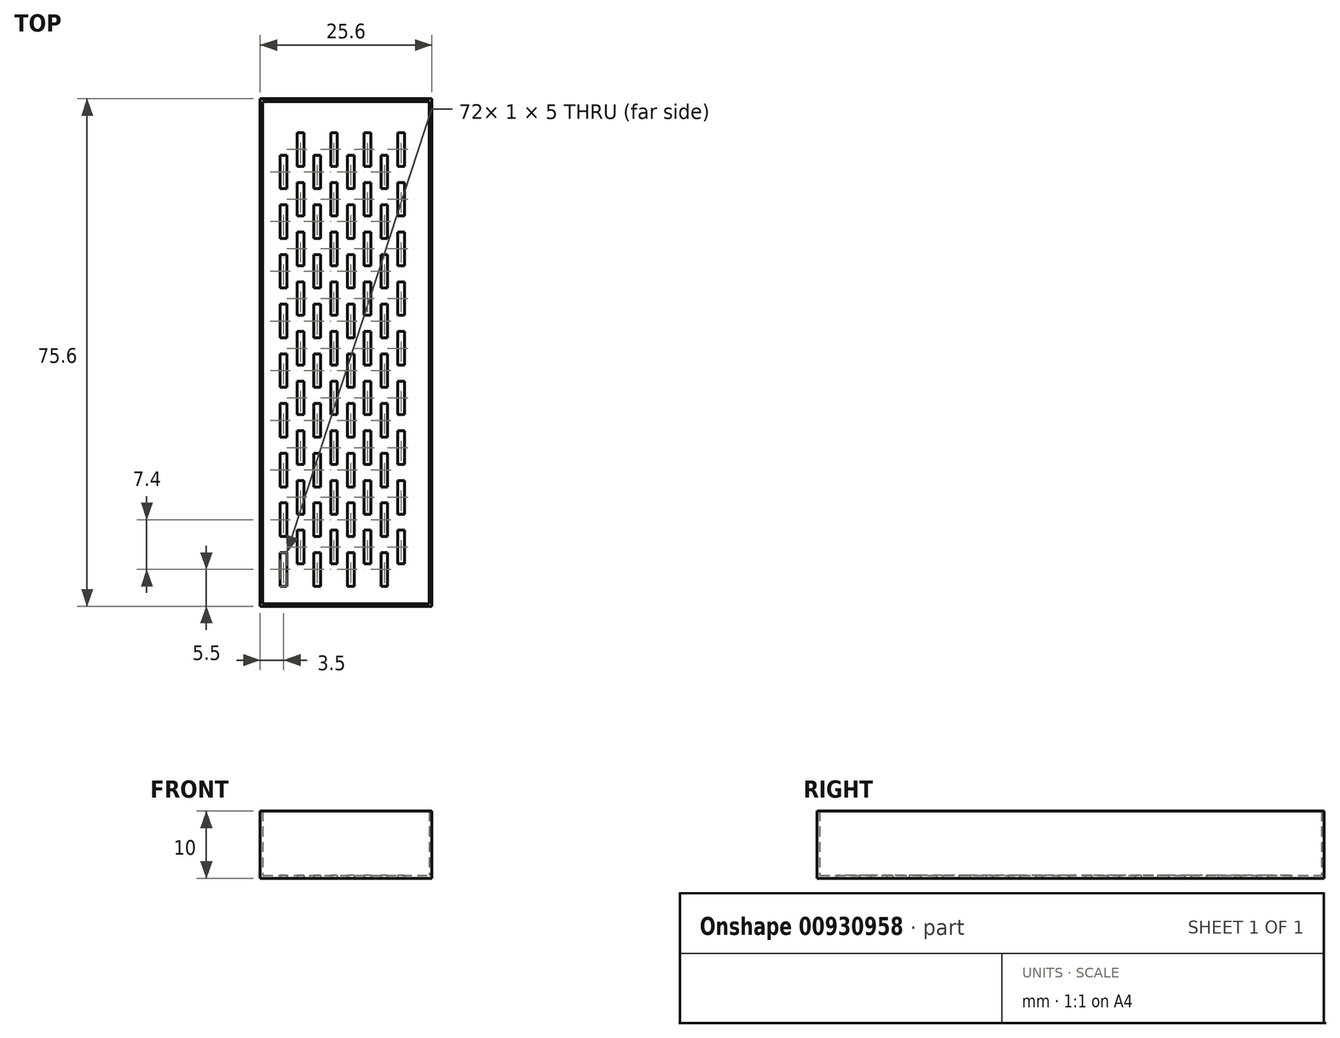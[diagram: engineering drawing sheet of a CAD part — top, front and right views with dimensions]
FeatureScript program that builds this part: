
annotation { "Feature Type Name" : "Feature", "Feature Type Description" : "" }
export const myFeature = defineFeature(function(context is Context, id is Id, definition is map)
    precondition{}
    {
        {
            assignVariable(context, id + "F0", {"name" : "wall", "anyValue" : 0.4});
        }
        {
            var Q0;
            Q0=qCreatedBy(makeId("Top.planeOp"),FACE);
            var sketch = newSketch(context, id + "F1", { "sketchPlane" : qUnion([Q0])});
            skLineSegment(sketch, "E0.bottom", {"start": v(0, 0) * mm, "end": v(25.6, 0) * mm});
            skLineSegment(sketch, "E0.top", {"start": v(0, 75.6) * mm, "end": v(25.6, 75.6) * mm});
            skLineSegment(sketch, "E0.left", {"start": v(0, 0) * mm, "end": v(0, 75.6) * mm});
            skLineSegment(sketch, "E0.right", {"start": v(25.6, 0) * mm, "end": v(25.6, 75.6) * mm});
            skSolve(sketch);
        }
        {
            var Q0;
            Q0 = qSketchRegion(id + "F1", true);
            extrude(context, id + "F2", {"entities" : qUnion([Q0]), "depth" : 10 * mm, "offsetDistance" : 25 * mm});
        }
        {
            var Q0;
            Q0=makeQuery(id+"F2.opExtrude","CAP_FACE",FACE,{"disambiguationData":[OSD([sQuery(id+"F1.wireOp",EDGE,"E0.bottom"),sQuery(id+"F1.wireOp",EDGE,"E0.top"),sQuery(id+"F1.wireOp",EDGE,"E0.left"),sQuery(id+"F1.wireOp",EDGE,"E0.right")])],"isStart":false});
            shell(context, id + "F3", {"entities" : qUnion([Q0]), "thickness" : (getVariable(context, 'wall')) * mm});
        }
        {
            var Q0;
            Q0=makeQuery(id+"F2.opExtrude","CAP_FACE",FACE,{"disambiguationData":[OSD([sQuery(id+"F1.wireOp",EDGE,"E0.bottom"),sQuery(id+"F1.wireOp",EDGE,"E0.top"),sQuery(id+"F1.wireOp",EDGE,"E0.left"),sQuery(id+"F1.wireOp",EDGE,"E0.right")])],"isStart":true});
            var sketch = newSketch(context, id + "F4", { "sketchPlane" : qUnion([Q0])});
            skLineSegment(sketch, "E1.bottom", {"start": v(3, -3) * mm, "end": v(4, -3) * mm});
            skLineSegment(sketch, "E1.top", {"start": v(3, -8) * mm, "end": v(4, -8) * mm});
            skLineSegment(sketch, "E1.left", {"start": v(3, -3) * mm, "end": v(3, -8) * mm});
            skLineSegment(sketch, "E1.right", {"start": v(4, -3) * mm, "end": v(4, -8) * mm});
            skLineSegment(sketch, "E2.bottom", {"start": v(5.5, -6.33) * mm, "end": v(6.5, -6.33) * mm});
            skLineSegment(sketch, "E2.top", {"start": v(5.5, -11.33) * mm, "end": v(6.5, -11.33) * mm});
            skLineSegment(sketch, "E2.left", {"start": v(5.5, -6.33) * mm, "end": v(5.5, -11.33) * mm});
            skLineSegment(sketch, "E2.right", {"start": v(6.5, -6.33) * mm, "end": v(6.5, -11.33) * mm});
            skLineSegment(sketch, "E3.0.1.0", {"start": v(5.5, -13.73) * mm, "end": v(5.5, -18.73) * mm});
            skLineSegment(sketch, "E3.0.1.1", {"start": v(3, -10.4) * mm, "end": v(4, -10.4) * mm});
            skLineSegment(sketch, "E3.0.1.2", {"start": v(6.5, -13.73) * mm, "end": v(6.5, -18.73) * mm});
            skLineSegment(sketch, "E3.0.1.3", {"start": v(5.5, -18.73) * mm, "end": v(6.5, -18.73) * mm});
            skLineSegment(sketch, "E3.0.1.4", {"start": v(5.5, -13.73) * mm, "end": v(6.5, -13.73) * mm});
            skLineSegment(sketch, "E3.0.1.5", {"start": v(3, -10.4) * mm, "end": v(3, -15.4) * mm});
            skLineSegment(sketch, "E3.0.1.6", {"start": v(3, -15.4) * mm, "end": v(4, -15.4) * mm});
            skLineSegment(sketch, "E3.0.1.7", {"start": v(4, -10.4) * mm, "end": v(4, -15.4) * mm});
            skLineSegment(sketch, "E3.0.2.0", {"start": v(5.5, -21.13) * mm, "end": v(5.5, -26.13) * mm});
            skLineSegment(sketch, "E3.0.2.1", {"start": v(3, -17.8) * mm, "end": v(4, -17.8) * mm});
            skLineSegment(sketch, "E3.0.2.2", {"start": v(6.5, -21.13) * mm, "end": v(6.5, -26.13) * mm});
            skLineSegment(sketch, "E3.0.2.3", {"start": v(5.5, -26.13) * mm, "end": v(6.5, -26.13) * mm});
            skLineSegment(sketch, "E3.0.2.4", {"start": v(5.5, -21.13) * mm, "end": v(6.5, -21.13) * mm});
            skLineSegment(sketch, "E3.0.2.5", {"start": v(3, -17.8) * mm, "end": v(3, -22.8) * mm});
            skLineSegment(sketch, "E3.0.2.6", {"start": v(3, -22.8) * mm, "end": v(4, -22.8) * mm});
            skLineSegment(sketch, "E3.0.2.7", {"start": v(4, -17.8) * mm, "end": v(4, -22.8) * mm});
            skLineSegment(sketch, "E3.0.3.0", {"start": v(5.5, -28.53) * mm, "end": v(5.5, -33.53) * mm});
            skLineSegment(sketch, "E3.0.3.1", {"start": v(3, -25.2) * mm, "end": v(4, -25.2) * mm});
            skLineSegment(sketch, "E3.0.3.2", {"start": v(6.5, -28.53) * mm, "end": v(6.5, -33.53) * mm});
            skLineSegment(sketch, "E3.0.3.3", {"start": v(5.5, -33.53) * mm, "end": v(6.5, -33.53) * mm});
            skLineSegment(sketch, "E3.0.3.4", {"start": v(5.5, -28.53) * mm, "end": v(6.5, -28.53) * mm});
            skLineSegment(sketch, "E3.0.3.5", {"start": v(3, -25.2) * mm, "end": v(3, -30.2) * mm});
            skLineSegment(sketch, "E3.0.3.6", {"start": v(3, -30.2) * mm, "end": v(4, -30.2) * mm});
            skLineSegment(sketch, "E3.0.3.7", {"start": v(4, -25.2) * mm, "end": v(4, -30.2) * mm});
            skLineSegment(sketch, "E3.0.4.0", {"start": v(5.5, -35.93) * mm, "end": v(5.5, -40.93) * mm});
            skLineSegment(sketch, "E3.0.4.1", {"start": v(3, -32.6) * mm, "end": v(4, -32.6) * mm});
            skLineSegment(sketch, "E3.0.4.2", {"start": v(6.5, -35.93) * mm, "end": v(6.5, -40.93) * mm});
            skLineSegment(sketch, "E3.0.4.3", {"start": v(5.5, -40.93) * mm, "end": v(6.5, -40.93) * mm});
            skLineSegment(sketch, "E3.0.4.4", {"start": v(5.5, -35.93) * mm, "end": v(6.5, -35.93) * mm});
            skLineSegment(sketch, "E3.0.4.5", {"start": v(3, -32.6) * mm, "end": v(3, -37.6) * mm});
            skLineSegment(sketch, "E3.0.4.6", {"start": v(3, -37.6) * mm, "end": v(4, -37.6) * mm});
            skLineSegment(sketch, "E3.0.4.7", {"start": v(4, -32.6) * mm, "end": v(4, -37.6) * mm});
            skLineSegment(sketch, "E3.0.5.0", {"start": v(5.5, -43.33) * mm, "end": v(5.5, -48.33) * mm});
            skLineSegment(sketch, "E3.0.5.1", {"start": v(3, -40) * mm, "end": v(4, -40) * mm});
            skLineSegment(sketch, "E3.0.5.2", {"start": v(6.5, -43.33) * mm, "end": v(6.5, -48.33) * mm});
            skLineSegment(sketch, "E3.0.5.3", {"start": v(5.5, -48.33) * mm, "end": v(6.5, -48.33) * mm});
            skLineSegment(sketch, "E3.0.5.4", {"start": v(5.5, -43.33) * mm, "end": v(6.5, -43.33) * mm});
            skLineSegment(sketch, "E3.0.5.5", {"start": v(3, -40) * mm, "end": v(3, -45) * mm});
            skLineSegment(sketch, "E3.0.5.6", {"start": v(3, -45) * mm, "end": v(4, -45) * mm});
            skLineSegment(sketch, "E3.0.5.7", {"start": v(4, -40) * mm, "end": v(4, -45) * mm});
            skLineSegment(sketch, "E3.0.6.0", {"start": v(5.5, -50.73) * mm, "end": v(5.5, -55.73) * mm});
            skLineSegment(sketch, "E3.0.6.1", {"start": v(3, -47.4) * mm, "end": v(4, -47.4) * mm});
            skLineSegment(sketch, "E3.0.6.2", {"start": v(6.5, -50.73) * mm, "end": v(6.5, -55.73) * mm});
            skLineSegment(sketch, "E3.0.6.3", {"start": v(5.5, -55.73) * mm, "end": v(6.5, -55.73) * mm});
            skLineSegment(sketch, "E3.0.6.4", {"start": v(5.5, -50.73) * mm, "end": v(6.5, -50.73) * mm});
            skLineSegment(sketch, "E3.0.6.5", {"start": v(3, -47.4) * mm, "end": v(3, -52.4) * mm});
            skLineSegment(sketch, "E3.0.6.6", {"start": v(3, -52.4) * mm, "end": v(4, -52.4) * mm});
            skLineSegment(sketch, "E3.0.6.7", {"start": v(4, -47.4) * mm, "end": v(4, -52.4) * mm});
            skLineSegment(sketch, "E3.0.7.0", {"start": v(5.5, -58.13) * mm, "end": v(5.5, -63.13) * mm});
            skLineSegment(sketch, "E3.0.7.1", {"start": v(3, -54.8) * mm, "end": v(4, -54.8) * mm});
            skLineSegment(sketch, "E3.0.7.2", {"start": v(6.5, -58.13) * mm, "end": v(6.5, -63.13) * mm});
            skLineSegment(sketch, "E3.0.7.3", {"start": v(5.5, -63.13) * mm, "end": v(6.5, -63.13) * mm});
            skLineSegment(sketch, "E3.0.7.4", {"start": v(5.5, -58.13) * mm, "end": v(6.5, -58.13) * mm});
            skLineSegment(sketch, "E3.0.7.5", {"start": v(3, -54.8) * mm, "end": v(3, -59.8) * mm});
            skLineSegment(sketch, "E3.0.7.6", {"start": v(3, -59.8) * mm, "end": v(4, -59.8) * mm});
            skLineSegment(sketch, "E3.0.7.7", {"start": v(4, -54.8) * mm, "end": v(4, -59.8) * mm});
            skLineSegment(sketch, "E3.0.8.0", {"start": v(5.5, -65.53) * mm, "end": v(5.5, -70.53) * mm});
            skLineSegment(sketch, "E3.0.8.1", {"start": v(3, -62.2) * mm, "end": v(4, -62.2) * mm});
            skLineSegment(sketch, "E3.0.8.2", {"start": v(6.5, -65.53) * mm, "end": v(6.5, -70.53) * mm});
            skLineSegment(sketch, "E3.0.8.3", {"start": v(5.5, -70.53) * mm, "end": v(6.5, -70.53) * mm});
            skLineSegment(sketch, "E3.0.8.4", {"start": v(5.5, -65.53) * mm, "end": v(6.5, -65.53) * mm});
            skLineSegment(sketch, "E3.0.8.5", {"start": v(3, -62.2) * mm, "end": v(3, -67.2) * mm});
            skLineSegment(sketch, "E3.0.8.6", {"start": v(3, -67.2) * mm, "end": v(4, -67.2) * mm});
            skLineSegment(sketch, "E3.0.8.7", {"start": v(4, -62.2) * mm, "end": v(4, -67.2) * mm});
            skLineSegment(sketch, "E3.1.0.0", {"start": v(10.5, -6.33) * mm, "end": v(10.5, -11.33) * mm});
            skLineSegment(sketch, "E3.1.0.1", {"start": v(8, -3) * mm, "end": v(9, -3) * mm});
            skLineSegment(sketch, "E3.1.0.2", {"start": v(11.5, -6.33) * mm, "end": v(11.5, -11.33) * mm});
            skLineSegment(sketch, "E3.1.0.3", {"start": v(10.5, -11.33) * mm, "end": v(11.5, -11.33) * mm});
            skLineSegment(sketch, "E3.1.0.4", {"start": v(10.5, -6.33) * mm, "end": v(11.5, -6.33) * mm});
            skLineSegment(sketch, "E3.1.0.5", {"start": v(8, -3) * mm, "end": v(8, -8) * mm});
            skLineSegment(sketch, "E3.1.0.6", {"start": v(8, -8) * mm, "end": v(9, -8) * mm});
            skLineSegment(sketch, "E3.1.0.7", {"start": v(9, -3) * mm, "end": v(9, -8) * mm});
            skLineSegment(sketch, "E3.1.1.0", {"start": v(10.5, -13.73) * mm, "end": v(10.5, -18.73) * mm});
            skLineSegment(sketch, "E3.1.1.1", {"start": v(8, -10.4) * mm, "end": v(9, -10.4) * mm});
            skLineSegment(sketch, "E3.1.1.2", {"start": v(11.5, -13.73) * mm, "end": v(11.5, -18.73) * mm});
            skLineSegment(sketch, "E3.1.1.3", {"start": v(10.5, -18.73) * mm, "end": v(11.5, -18.73) * mm});
            skLineSegment(sketch, "E3.1.1.4", {"start": v(10.5, -13.73) * mm, "end": v(11.5, -13.73) * mm});
            skLineSegment(sketch, "E3.1.1.5", {"start": v(8, -10.4) * mm, "end": v(8, -15.4) * mm});
            skLineSegment(sketch, "E3.1.1.6", {"start": v(8, -15.4) * mm, "end": v(9, -15.4) * mm});
            skLineSegment(sketch, "E3.1.1.7", {"start": v(9, -10.4) * mm, "end": v(9, -15.4) * mm});
            skLineSegment(sketch, "E3.1.2.0", {"start": v(10.5, -21.13) * mm, "end": v(10.5, -26.13) * mm});
            skLineSegment(sketch, "E3.1.2.1", {"start": v(8, -17.8) * mm, "end": v(9, -17.8) * mm});
            skLineSegment(sketch, "E3.1.2.2", {"start": v(11.5, -21.13) * mm, "end": v(11.5, -26.13) * mm});
            skLineSegment(sketch, "E3.1.2.3", {"start": v(10.5, -26.13) * mm, "end": v(11.5, -26.13) * mm});
            skLineSegment(sketch, "E3.1.2.4", {"start": v(10.5, -21.13) * mm, "end": v(11.5, -21.13) * mm});
            skLineSegment(sketch, "E3.1.2.5", {"start": v(8, -17.8) * mm, "end": v(8, -22.8) * mm});
            skLineSegment(sketch, "E3.1.2.6", {"start": v(8, -22.8) * mm, "end": v(9, -22.8) * mm});
            skLineSegment(sketch, "E3.1.2.7", {"start": v(9, -17.8) * mm, "end": v(9, -22.8) * mm});
            skLineSegment(sketch, "E3.1.3.0", {"start": v(10.5, -28.53) * mm, "end": v(10.5, -33.53) * mm});
            skLineSegment(sketch, "E3.1.3.1", {"start": v(8, -25.2) * mm, "end": v(9, -25.2) * mm});
            skLineSegment(sketch, "E3.1.3.2", {"start": v(11.5, -28.53) * mm, "end": v(11.5, -33.53) * mm});
            skLineSegment(sketch, "E3.1.3.3", {"start": v(10.5, -33.53) * mm, "end": v(11.5, -33.53) * mm});
            skLineSegment(sketch, "E3.1.3.4", {"start": v(10.5, -28.53) * mm, "end": v(11.5, -28.53) * mm});
            skLineSegment(sketch, "E3.1.3.5", {"start": v(8, -25.2) * mm, "end": v(8, -30.2) * mm});
            skLineSegment(sketch, "E3.1.3.6", {"start": v(8, -30.2) * mm, "end": v(9, -30.2) * mm});
            skLineSegment(sketch, "E3.1.3.7", {"start": v(9, -25.2) * mm, "end": v(9, -30.2) * mm});
            skLineSegment(sketch, "E3.1.4.0", {"start": v(10.5, -35.93) * mm, "end": v(10.5, -40.93) * mm});
            skLineSegment(sketch, "E3.1.4.1", {"start": v(8, -32.6) * mm, "end": v(9, -32.6) * mm});
            skLineSegment(sketch, "E3.1.4.2", {"start": v(11.5, -35.93) * mm, "end": v(11.5, -40.93) * mm});
            skLineSegment(sketch, "E3.1.4.3", {"start": v(10.5, -40.93) * mm, "end": v(11.5, -40.93) * mm});
            skLineSegment(sketch, "E3.1.4.4", {"start": v(10.5, -35.93) * mm, "end": v(11.5, -35.93) * mm});
            skLineSegment(sketch, "E3.1.4.5", {"start": v(8, -32.6) * mm, "end": v(8, -37.6) * mm});
            skLineSegment(sketch, "E3.1.4.6", {"start": v(8, -37.6) * mm, "end": v(9, -37.6) * mm});
            skLineSegment(sketch, "E3.1.4.7", {"start": v(9, -32.6) * mm, "end": v(9, -37.6) * mm});
            skLineSegment(sketch, "E3.1.5.0", {"start": v(10.5, -43.33) * mm, "end": v(10.5, -48.33) * mm});
            skLineSegment(sketch, "E3.1.5.1", {"start": v(8, -40) * mm, "end": v(9, -40) * mm});
            skLineSegment(sketch, "E3.1.5.2", {"start": v(11.5, -43.33) * mm, "end": v(11.5, -48.33) * mm});
            skLineSegment(sketch, "E3.1.5.3", {"start": v(10.5, -48.33) * mm, "end": v(11.5, -48.33) * mm});
            skLineSegment(sketch, "E3.1.5.4", {"start": v(10.5, -43.33) * mm, "end": v(11.5, -43.33) * mm});
            skLineSegment(sketch, "E3.1.5.5", {"start": v(8, -40) * mm, "end": v(8, -45) * mm});
            skLineSegment(sketch, "E3.1.5.6", {"start": v(8, -45) * mm, "end": v(9, -45) * mm});
            skLineSegment(sketch, "E3.1.5.7", {"start": v(9, -40) * mm, "end": v(9, -45) * mm});
            skLineSegment(sketch, "E3.1.6.0", {"start": v(10.5, -50.73) * mm, "end": v(10.5, -55.73) * mm});
            skLineSegment(sketch, "E3.1.6.1", {"start": v(8, -47.4) * mm, "end": v(9, -47.4) * mm});
            skLineSegment(sketch, "E3.1.6.2", {"start": v(11.5, -50.73) * mm, "end": v(11.5, -55.73) * mm});
            skLineSegment(sketch, "E3.1.6.3", {"start": v(10.5, -55.73) * mm, "end": v(11.5, -55.73) * mm});
            skLineSegment(sketch, "E3.1.6.4", {"start": v(10.5, -50.73) * mm, "end": v(11.5, -50.73) * mm});
            skLineSegment(sketch, "E3.1.6.5", {"start": v(8, -47.4) * mm, "end": v(8, -52.4) * mm});
            skLineSegment(sketch, "E3.1.6.6", {"start": v(8, -52.4) * mm, "end": v(9, -52.4) * mm});
            skLineSegment(sketch, "E3.1.6.7", {"start": v(9, -47.4) * mm, "end": v(9, -52.4) * mm});
            skLineSegment(sketch, "E3.1.7.0", {"start": v(10.5, -58.13) * mm, "end": v(10.5, -63.13) * mm});
            skLineSegment(sketch, "E3.1.7.1", {"start": v(8, -54.8) * mm, "end": v(9, -54.8) * mm});
            skLineSegment(sketch, "E3.1.7.2", {"start": v(11.5, -58.13) * mm, "end": v(11.5, -63.13) * mm});
            skLineSegment(sketch, "E3.1.7.3", {"start": v(10.5, -63.13) * mm, "end": v(11.5, -63.13) * mm});
            skLineSegment(sketch, "E3.1.7.4", {"start": v(10.5, -58.13) * mm, "end": v(11.5, -58.13) * mm});
            skLineSegment(sketch, "E3.1.7.5", {"start": v(8, -54.8) * mm, "end": v(8, -59.8) * mm});
            skLineSegment(sketch, "E3.1.7.6", {"start": v(8, -59.8) * mm, "end": v(9, -59.8) * mm});
            skLineSegment(sketch, "E3.1.7.7", {"start": v(9, -54.8) * mm, "end": v(9, -59.8) * mm});
            skLineSegment(sketch, "E3.1.8.0", {"start": v(10.5, -65.53) * mm, "end": v(10.5, -70.53) * mm});
            skLineSegment(sketch, "E3.1.8.1", {"start": v(8, -62.2) * mm, "end": v(9, -62.2) * mm});
            skLineSegment(sketch, "E3.1.8.2", {"start": v(11.5, -65.53) * mm, "end": v(11.5, -70.53) * mm});
            skLineSegment(sketch, "E3.1.8.3", {"start": v(10.5, -70.53) * mm, "end": v(11.5, -70.53) * mm});
            skLineSegment(sketch, "E3.1.8.4", {"start": v(10.5, -65.53) * mm, "end": v(11.5, -65.53) * mm});
            skLineSegment(sketch, "E3.1.8.5", {"start": v(8, -62.2) * mm, "end": v(8, -67.2) * mm});
            skLineSegment(sketch, "E3.1.8.6", {"start": v(8, -67.2) * mm, "end": v(9, -67.2) * mm});
            skLineSegment(sketch, "E3.1.8.7", {"start": v(9, -62.2) * mm, "end": v(9, -67.2) * mm});
            skLineSegment(sketch, "E3.2.0.0", {"start": v(15.5, -6.33) * mm, "end": v(15.5, -11.33) * mm});
            skLineSegment(sketch, "E3.2.0.1", {"start": v(13, -3) * mm, "end": v(14, -3) * mm});
            skLineSegment(sketch, "E3.2.0.2", {"start": v(16.5, -6.33) * mm, "end": v(16.5, -11.33) * mm});
            skLineSegment(sketch, "E3.2.0.3", {"start": v(15.5, -11.33) * mm, "end": v(16.5, -11.33) * mm});
            skLineSegment(sketch, "E3.2.0.4", {"start": v(15.5, -6.33) * mm, "end": v(16.5, -6.33) * mm});
            skLineSegment(sketch, "E3.2.0.5", {"start": v(13, -3) * mm, "end": v(13, -8) * mm});
            skLineSegment(sketch, "E3.2.0.6", {"start": v(13, -8) * mm, "end": v(14, -8) * mm});
            skLineSegment(sketch, "E3.2.0.7", {"start": v(14, -3) * mm, "end": v(14, -8) * mm});
            skLineSegment(sketch, "E3.2.1.0", {"start": v(15.5, -13.73) * mm, "end": v(15.5, -18.73) * mm});
            skLineSegment(sketch, "E3.2.1.1", {"start": v(13, -10.4) * mm, "end": v(14, -10.4) * mm});
            skLineSegment(sketch, "E3.2.1.2", {"start": v(16.5, -13.73) * mm, "end": v(16.5, -18.73) * mm});
            skLineSegment(sketch, "E3.2.1.3", {"start": v(15.5, -18.73) * mm, "end": v(16.5, -18.73) * mm});
            skLineSegment(sketch, "E3.2.1.4", {"start": v(15.5, -13.73) * mm, "end": v(16.5, -13.73) * mm});
            skLineSegment(sketch, "E3.2.1.5", {"start": v(13, -10.4) * mm, "end": v(13, -15.4) * mm});
            skLineSegment(sketch, "E3.2.1.6", {"start": v(13, -15.4) * mm, "end": v(14, -15.4) * mm});
            skLineSegment(sketch, "E3.2.1.7", {"start": v(14, -10.4) * mm, "end": v(14, -15.4) * mm});
            skLineSegment(sketch, "E3.2.2.0", {"start": v(15.5, -21.13) * mm, "end": v(15.5, -26.13) * mm});
            skLineSegment(sketch, "E3.2.2.1", {"start": v(13, -17.8) * mm, "end": v(14, -17.8) * mm});
            skLineSegment(sketch, "E3.2.2.2", {"start": v(16.5, -21.13) * mm, "end": v(16.5, -26.13) * mm});
            skLineSegment(sketch, "E3.2.2.3", {"start": v(15.5, -26.13) * mm, "end": v(16.5, -26.13) * mm});
            skLineSegment(sketch, "E3.2.2.4", {"start": v(15.5, -21.13) * mm, "end": v(16.5, -21.13) * mm});
            skLineSegment(sketch, "E3.2.2.5", {"start": v(13, -17.8) * mm, "end": v(13, -22.8) * mm});
            skLineSegment(sketch, "E3.2.2.6", {"start": v(13, -22.8) * mm, "end": v(14, -22.8) * mm});
            skLineSegment(sketch, "E3.2.2.7", {"start": v(14, -17.8) * mm, "end": v(14, -22.8) * mm});
            skLineSegment(sketch, "E3.2.3.0", {"start": v(15.5, -28.53) * mm, "end": v(15.5, -33.53) * mm});
            skLineSegment(sketch, "E3.2.3.1", {"start": v(13, -25.2) * mm, "end": v(14, -25.2) * mm});
            skLineSegment(sketch, "E3.2.3.2", {"start": v(16.5, -28.53) * mm, "end": v(16.5, -33.53) * mm});
            skLineSegment(sketch, "E3.2.3.3", {"start": v(15.5, -33.53) * mm, "end": v(16.5, -33.53) * mm});
            skLineSegment(sketch, "E3.2.3.4", {"start": v(15.5, -28.53) * mm, "end": v(16.5, -28.53) * mm});
            skLineSegment(sketch, "E3.2.3.5", {"start": v(13, -25.2) * mm, "end": v(13, -30.2) * mm});
            skLineSegment(sketch, "E3.2.3.6", {"start": v(13, -30.2) * mm, "end": v(14, -30.2) * mm});
            skLineSegment(sketch, "E3.2.3.7", {"start": v(14, -25.2) * mm, "end": v(14, -30.2) * mm});
            skLineSegment(sketch, "E3.2.4.0", {"start": v(15.5, -35.93) * mm, "end": v(15.5, -40.93) * mm});
            skLineSegment(sketch, "E3.2.4.1", {"start": v(13, -32.6) * mm, "end": v(14, -32.6) * mm});
            skLineSegment(sketch, "E3.2.4.2", {"start": v(16.5, -35.93) * mm, "end": v(16.5, -40.93) * mm});
            skLineSegment(sketch, "E3.2.4.3", {"start": v(15.5, -40.93) * mm, "end": v(16.5, -40.93) * mm});
            skLineSegment(sketch, "E3.2.4.4", {"start": v(15.5, -35.93) * mm, "end": v(16.5, -35.93) * mm});
            skLineSegment(sketch, "E3.2.4.5", {"start": v(13, -32.6) * mm, "end": v(13, -37.6) * mm});
            skLineSegment(sketch, "E3.2.4.6", {"start": v(13, -37.6) * mm, "end": v(14, -37.6) * mm});
            skLineSegment(sketch, "E3.2.4.7", {"start": v(14, -32.6) * mm, "end": v(14, -37.6) * mm});
            skLineSegment(sketch, "E3.2.5.0", {"start": v(15.5, -43.33) * mm, "end": v(15.5, -48.33) * mm});
            skLineSegment(sketch, "E3.2.5.1", {"start": v(13, -40) * mm, "end": v(14, -40) * mm});
            skLineSegment(sketch, "E3.2.5.2", {"start": v(16.5, -43.33) * mm, "end": v(16.5, -48.33) * mm});
            skLineSegment(sketch, "E3.2.5.3", {"start": v(15.5, -48.33) * mm, "end": v(16.5, -48.33) * mm});
            skLineSegment(sketch, "E3.2.5.4", {"start": v(15.5, -43.33) * mm, "end": v(16.5, -43.33) * mm});
            skLineSegment(sketch, "E3.2.5.5", {"start": v(13, -40) * mm, "end": v(13, -45) * mm});
            skLineSegment(sketch, "E3.2.5.6", {"start": v(13, -45) * mm, "end": v(14, -45) * mm});
            skLineSegment(sketch, "E3.2.5.7", {"start": v(14, -40) * mm, "end": v(14, -45) * mm});
            skLineSegment(sketch, "E3.2.6.0", {"start": v(15.5, -50.73) * mm, "end": v(15.5, -55.73) * mm});
            skLineSegment(sketch, "E3.2.6.1", {"start": v(13, -47.4) * mm, "end": v(14, -47.4) * mm});
            skLineSegment(sketch, "E3.2.6.2", {"start": v(16.5, -50.73) * mm, "end": v(16.5, -55.73) * mm});
            skLineSegment(sketch, "E3.2.6.3", {"start": v(15.5, -55.73) * mm, "end": v(16.5, -55.73) * mm});
            skLineSegment(sketch, "E3.2.6.4", {"start": v(15.5, -50.73) * mm, "end": v(16.5, -50.73) * mm});
            skLineSegment(sketch, "E3.2.6.5", {"start": v(13, -47.4) * mm, "end": v(13, -52.4) * mm});
            skLineSegment(sketch, "E3.2.6.6", {"start": v(13, -52.4) * mm, "end": v(14, -52.4) * mm});
            skLineSegment(sketch, "E3.2.6.7", {"start": v(14, -47.4) * mm, "end": v(14, -52.4) * mm});
            skLineSegment(sketch, "E3.2.7.0", {"start": v(15.5, -58.13) * mm, "end": v(15.5, -63.13) * mm});
            skLineSegment(sketch, "E3.2.7.1", {"start": v(13, -54.8) * mm, "end": v(14, -54.8) * mm});
            skLineSegment(sketch, "E3.2.7.2", {"start": v(16.5, -58.13) * mm, "end": v(16.5, -63.13) * mm});
            skLineSegment(sketch, "E3.2.7.3", {"start": v(15.5, -63.13) * mm, "end": v(16.5, -63.13) * mm});
            skLineSegment(sketch, "E3.2.7.4", {"start": v(15.5, -58.13) * mm, "end": v(16.5, -58.13) * mm});
            skLineSegment(sketch, "E3.2.7.5", {"start": v(13, -54.8) * mm, "end": v(13, -59.8) * mm});
            skLineSegment(sketch, "E3.2.7.6", {"start": v(13, -59.8) * mm, "end": v(14, -59.8) * mm});
            skLineSegment(sketch, "E3.2.7.7", {"start": v(14, -54.8) * mm, "end": v(14, -59.8) * mm});
            skLineSegment(sketch, "E3.2.8.0", {"start": v(15.5, -65.53) * mm, "end": v(15.5, -70.53) * mm});
            skLineSegment(sketch, "E3.2.8.1", {"start": v(13, -62.2) * mm, "end": v(14, -62.2) * mm});
            skLineSegment(sketch, "E3.2.8.2", {"start": v(16.5, -65.53) * mm, "end": v(16.5, -70.53) * mm});
            skLineSegment(sketch, "E3.2.8.3", {"start": v(15.5, -70.53) * mm, "end": v(16.5, -70.53) * mm});
            skLineSegment(sketch, "E3.2.8.4", {"start": v(15.5, -65.53) * mm, "end": v(16.5, -65.53) * mm});
            skLineSegment(sketch, "E3.2.8.5", {"start": v(13, -62.2) * mm, "end": v(13, -67.2) * mm});
            skLineSegment(sketch, "E3.2.8.6", {"start": v(13, -67.2) * mm, "end": v(14, -67.2) * mm});
            skLineSegment(sketch, "E3.2.8.7", {"start": v(14, -62.2) * mm, "end": v(14, -67.2) * mm});
            skLineSegment(sketch, "E3.3.0.0", {"start": v(20.5, -6.33) * mm, "end": v(20.5, -11.33) * mm});
            skLineSegment(sketch, "E3.3.0.1", {"start": v(18, -3) * mm, "end": v(19, -3) * mm});
            skLineSegment(sketch, "E3.3.0.2", {"start": v(21.5, -6.33) * mm, "end": v(21.5, -11.33) * mm});
            skLineSegment(sketch, "E3.3.0.3", {"start": v(20.5, -11.33) * mm, "end": v(21.5, -11.33) * mm});
            skLineSegment(sketch, "E3.3.0.4", {"start": v(20.5, -6.33) * mm, "end": v(21.5, -6.33) * mm});
            skLineSegment(sketch, "E3.3.0.5", {"start": v(18, -3) * mm, "end": v(18, -8) * mm});
            skLineSegment(sketch, "E3.3.0.6", {"start": v(18, -8) * mm, "end": v(19, -8) * mm});
            skLineSegment(sketch, "E3.3.0.7", {"start": v(19, -3) * mm, "end": v(19, -8) * mm});
            skLineSegment(sketch, "E3.3.1.0", {"start": v(20.5, -13.73) * mm, "end": v(20.5, -18.73) * mm});
            skLineSegment(sketch, "E3.3.1.1", {"start": v(18, -10.4) * mm, "end": v(19, -10.4) * mm});
            skLineSegment(sketch, "E3.3.1.2", {"start": v(21.5, -13.73) * mm, "end": v(21.5, -18.73) * mm});
            skLineSegment(sketch, "E3.3.1.3", {"start": v(20.5, -18.73) * mm, "end": v(21.5, -18.73) * mm});
            skLineSegment(sketch, "E3.3.1.4", {"start": v(20.5, -13.73) * mm, "end": v(21.5, -13.73) * mm});
            skLineSegment(sketch, "E3.3.1.5", {"start": v(18, -10.4) * mm, "end": v(18, -15.4) * mm});
            skLineSegment(sketch, "E3.3.1.6", {"start": v(18, -15.4) * mm, "end": v(19, -15.4) * mm});
            skLineSegment(sketch, "E3.3.1.7", {"start": v(19, -10.4) * mm, "end": v(19, -15.4) * mm});
            skLineSegment(sketch, "E3.3.2.0", {"start": v(20.5, -21.13) * mm, "end": v(20.5, -26.13) * mm});
            skLineSegment(sketch, "E3.3.2.1", {"start": v(18, -17.8) * mm, "end": v(19, -17.8) * mm});
            skLineSegment(sketch, "E3.3.2.2", {"start": v(21.5, -21.13) * mm, "end": v(21.5, -26.13) * mm});
            skLineSegment(sketch, "E3.3.2.3", {"start": v(20.5, -26.13) * mm, "end": v(21.5, -26.13) * mm});
            skLineSegment(sketch, "E3.3.2.4", {"start": v(20.5, -21.13) * mm, "end": v(21.5, -21.13) * mm});
            skLineSegment(sketch, "E3.3.2.5", {"start": v(18, -17.8) * mm, "end": v(18, -22.8) * mm});
            skLineSegment(sketch, "E3.3.2.6", {"start": v(18, -22.8) * mm, "end": v(19, -22.8) * mm});
            skLineSegment(sketch, "E3.3.2.7", {"start": v(19, -17.8) * mm, "end": v(19, -22.8) * mm});
            skLineSegment(sketch, "E3.3.3.0", {"start": v(20.5, -28.53) * mm, "end": v(20.5, -33.53) * mm});
            skLineSegment(sketch, "E3.3.3.1", {"start": v(18, -25.2) * mm, "end": v(19, -25.2) * mm});
            skLineSegment(sketch, "E3.3.3.2", {"start": v(21.5, -28.53) * mm, "end": v(21.5, -33.53) * mm});
            skLineSegment(sketch, "E3.3.3.3", {"start": v(20.5, -33.53) * mm, "end": v(21.5, -33.53) * mm});
            skLineSegment(sketch, "E3.3.3.4", {"start": v(20.5, -28.53) * mm, "end": v(21.5, -28.53) * mm});
            skLineSegment(sketch, "E3.3.3.5", {"start": v(18, -25.2) * mm, "end": v(18, -30.2) * mm});
            skLineSegment(sketch, "E3.3.3.6", {"start": v(18, -30.2) * mm, "end": v(19, -30.2) * mm});
            skLineSegment(sketch, "E3.3.3.7", {"start": v(19, -25.2) * mm, "end": v(19, -30.2) * mm});
            skLineSegment(sketch, "E3.3.4.0", {"start": v(20.5, -35.93) * mm, "end": v(20.5, -40.93) * mm});
            skLineSegment(sketch, "E3.3.4.1", {"start": v(18, -32.6) * mm, "end": v(19, -32.6) * mm});
            skLineSegment(sketch, "E3.3.4.2", {"start": v(21.5, -35.93) * mm, "end": v(21.5, -40.93) * mm});
            skLineSegment(sketch, "E3.3.4.3", {"start": v(20.5, -40.93) * mm, "end": v(21.5, -40.93) * mm});
            skLineSegment(sketch, "E3.3.4.4", {"start": v(20.5, -35.93) * mm, "end": v(21.5, -35.93) * mm});
            skLineSegment(sketch, "E3.3.4.5", {"start": v(18, -32.6) * mm, "end": v(18, -37.6) * mm});
            skLineSegment(sketch, "E3.3.4.6", {"start": v(18, -37.6) * mm, "end": v(19, -37.6) * mm});
            skLineSegment(sketch, "E3.3.4.7", {"start": v(19, -32.6) * mm, "end": v(19, -37.6) * mm});
            skLineSegment(sketch, "E3.3.5.0", {"start": v(20.5, -43.33) * mm, "end": v(20.5, -48.33) * mm});
            skLineSegment(sketch, "E3.3.5.1", {"start": v(18, -40) * mm, "end": v(19, -40) * mm});
            skLineSegment(sketch, "E3.3.5.2", {"start": v(21.5, -43.33) * mm, "end": v(21.5, -48.33) * mm});
            skLineSegment(sketch, "E3.3.5.3", {"start": v(20.5, -48.33) * mm, "end": v(21.5, -48.33) * mm});
            skLineSegment(sketch, "E3.3.5.4", {"start": v(20.5, -43.33) * mm, "end": v(21.5, -43.33) * mm});
            skLineSegment(sketch, "E3.3.5.5", {"start": v(18, -40) * mm, "end": v(18, -45) * mm});
            skLineSegment(sketch, "E3.3.5.6", {"start": v(18, -45) * mm, "end": v(19, -45) * mm});
            skLineSegment(sketch, "E3.3.5.7", {"start": v(19, -40) * mm, "end": v(19, -45) * mm});
            skLineSegment(sketch, "E3.3.6.0", {"start": v(20.5, -50.73) * mm, "end": v(20.5, -55.73) * mm});
            skLineSegment(sketch, "E3.3.6.1", {"start": v(18, -47.4) * mm, "end": v(19, -47.4) * mm});
            skLineSegment(sketch, "E3.3.6.2", {"start": v(21.5, -50.73) * mm, "end": v(21.5, -55.73) * mm});
            skLineSegment(sketch, "E3.3.6.3", {"start": v(20.5, -55.73) * mm, "end": v(21.5, -55.73) * mm});
            skLineSegment(sketch, "E3.3.6.4", {"start": v(20.5, -50.73) * mm, "end": v(21.5, -50.73) * mm});
            skLineSegment(sketch, "E3.3.6.5", {"start": v(18, -47.4) * mm, "end": v(18, -52.4) * mm});
            skLineSegment(sketch, "E3.3.6.6", {"start": v(18, -52.4) * mm, "end": v(19, -52.4) * mm});
            skLineSegment(sketch, "E3.3.6.7", {"start": v(19, -47.4) * mm, "end": v(19, -52.4) * mm});
            skLineSegment(sketch, "E3.3.7.0", {"start": v(20.5, -58.13) * mm, "end": v(20.5, -63.13) * mm});
            skLineSegment(sketch, "E3.3.7.1", {"start": v(18, -54.8) * mm, "end": v(19, -54.8) * mm});
            skLineSegment(sketch, "E3.3.7.2", {"start": v(21.5, -58.13) * mm, "end": v(21.5, -63.13) * mm});
            skLineSegment(sketch, "E3.3.7.3", {"start": v(20.5, -63.13) * mm, "end": v(21.5, -63.13) * mm});
            skLineSegment(sketch, "E3.3.7.4", {"start": v(20.5, -58.13) * mm, "end": v(21.5, -58.13) * mm});
            skLineSegment(sketch, "E3.3.7.5", {"start": v(18, -54.8) * mm, "end": v(18, -59.8) * mm});
            skLineSegment(sketch, "E3.3.7.6", {"start": v(18, -59.8) * mm, "end": v(19, -59.8) * mm});
            skLineSegment(sketch, "E3.3.7.7", {"start": v(19, -54.8) * mm, "end": v(19, -59.8) * mm});
            skLineSegment(sketch, "E3.3.8.0", {"start": v(20.5, -65.53) * mm, "end": v(20.5, -70.53) * mm});
            skLineSegment(sketch, "E3.3.8.1", {"start": v(18, -62.2) * mm, "end": v(19, -62.2) * mm});
            skLineSegment(sketch, "E3.3.8.2", {"start": v(21.5, -65.53) * mm, "end": v(21.5, -70.53) * mm});
            skLineSegment(sketch, "E3.3.8.3", {"start": v(20.5, -70.53) * mm, "end": v(21.5, -70.53) * mm});
            skLineSegment(sketch, "E3.3.8.4", {"start": v(20.5, -65.53) * mm, "end": v(21.5, -65.53) * mm});
            skLineSegment(sketch, "E3.3.8.5", {"start": v(18, -62.2) * mm, "end": v(18, -67.2) * mm});
            skLineSegment(sketch, "E3.3.8.6", {"start": v(18, -67.2) * mm, "end": v(19, -67.2) * mm});
            skLineSegment(sketch, "E3.3.8.7", {"start": v(19, -62.2) * mm, "end": v(19, -67.2) * mm});
            skLineSegment(sketch, "E3.direction1", {"start": v(5.5, -11.33) * mm, "end": v(10.5, -11.33) * mm, "construction": true});
            skLineSegment(sketch, "E3.direction2", {"start": v(5.5, -11.33) * mm, "end": v(5.5, -18.73) * mm, "construction": true});
            skSolve(sketch);
        }
        {
            var Q0;
            Q0 = qSketchRegion(id + "F4", true);
            extrude(context, id + "F5", {"entities" : qUnion([Q0]), "operationType" : NewBodyOperationType.REMOVE, "endBound" : BoundingType.THROUGH_ALL, "oppositeDirection" : true, "depth" : 25 * mm, "offsetDistance" : 25 * mm});
        }
    });
